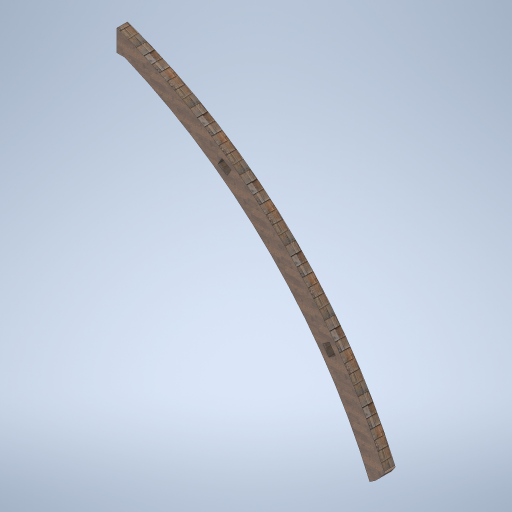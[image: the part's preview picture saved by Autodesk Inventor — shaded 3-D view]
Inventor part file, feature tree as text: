
AUTODESK INVENTOR PART (.ipt)
format: ipt  version: 2024.2 (Build 282272000, 272)  size: 340,992 bytes
history: native  units: mm
features: extrude x2, sketch x2, fillet x1
ambient origin geometry x8: Origin, YZ Plane, XZ Plane, XY Plane, X Axis, Y Axis, Z Axis, Center Point
bodies: Solid1 (feature_tree)
feature tree (5):
  extrude  "Extrusion1"  Depth=8500.0mm
  fillet  "Fillet2"  Radius=800.0mm
  extrude  "Extrusion2"  Depth=50.0mm
  sketch  "Sketch2"  dims[d5=8500.0mm d7=8500.0mm d8=800.0mm]
  sketch  "Sketch4"  dims[d9=100.0mm d10=100.0mm d11=0.0mm d12=0.0mm d15=50.0mm d16=200.0mm d17=30.0deg d18=150.0mm d19=200.0mm d20=9.599311mm d21=150.0mm d22=0.0mm d23=0.0mm]
